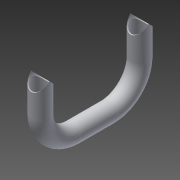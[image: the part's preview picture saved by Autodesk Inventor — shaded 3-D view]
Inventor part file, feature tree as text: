
AUTODESK INVENTOR PART (.ipt)
format: ipt  version: 2014 SP2 (Build 180246200, 246)  size: 179,200 bytes
history: native  units: mm
features: other x5, sketch x3, sweep x1, extrude x1
ambient origin geometry x8: Origin, YZ Plane, XZ Plane, XY Plane, X Axis, Y Axis, Z Axis, Center Point
bodies: Body1 (feature_tree)
feature tree (10):
  other  "Bryła1"
  other  "Płaszczyzna konstrukcyjna1"
  sketch  "Szkic1"
  other  "Płaszczyzna konstrukcyjna2"
  sweep  "Przeciągnięcie1"
  extrude  "Wyciągnięcie proste1"  Depth=1.5mm
  other  "Utwórz kombinację1"
  sketch  "Szkic2"
  sketch  "Szkic3"
  other  "Bryła2"
